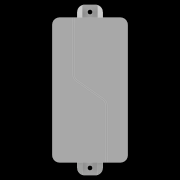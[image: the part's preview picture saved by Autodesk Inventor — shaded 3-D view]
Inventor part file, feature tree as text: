
AUTODESK INVENTOR PART (.ipt)
format: ipt  version: 2020 (Build 240168000, 168)  size: 243,712 bytes
history: native  units: in
note: dims shown in document units (in); Inventor stores cm internally (conversion verified against a paired STEP export)
features: other x9, extrude x4, fillet x2, mirror x2, loft x1
ambient origin geometry x8: Origin, YZ Plane, XZ Plane, XY Plane, X Axis, Y Axis, Z Axis, Center Point
bodies: Solid1 (feature_tree), Solid2 (feature_tree)
feature tree (18):
  extrude  "FishmanModern6Feature"  Depth=3.346in
  fillet  "FishmanModern6FilletsFeature"  Radius=1.481in
  other  "FishmanModern6LegPlane"
  extrude  "FishmanModern6LegsFeature"  Depth=3.063in
  loft  "FishmanModern6LegJoinFeature"
  mirror  "FishmanModern6Loft1Feature"
  mirror  "FishmanModern6Loft2Feature"
  extrude  "FishmanModern6JonFeature"  Depth=0.5in
  other  "FishmanModern6CombineFeature"
  fillet  "FishmanModern6LegFilletsFeatures"  Radius=0.25in
  extrude  "Extrusion8"  Depth=0.25in
  other  "FishmanModern6"
  other  "FishmanModern6SepPlane"
  other  "FishmanModern6Legs"
  other  "FishmanModern6LegLoft1"
  other  "FishmanModern6LegLoft2"
  other  "FishmanModern6Join"
  other  "FishmanModern6IndentFeature"
